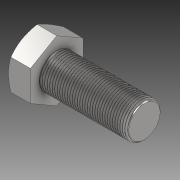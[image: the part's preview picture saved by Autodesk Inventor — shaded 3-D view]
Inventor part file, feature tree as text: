
AUTODESK INVENTOR PART (.ipt)
format: ipt  version: 2020 (Build 240168000, 168)  size: 557,568 bytes
history: mixed  units: in
note: dims shown in document units (in); Inventor stores cm internally (conversion verified against a paired STEP export)
features: revolve x1, imported_body x1
ambient origin geometry x8: Origin, YZ Plane, XZ Plane, XY Plane, X Axis, Y Axis, Z Axis, Center Point
bodies: Solid1 (imported_parasolid)
feature tree (2):
  revolve  "Revolve1"  [1 undecoded]
  imported_body  NMx_Import_Brep_tag  [imported B-rep: ~3 faces, bbox_mm=None]
note: 1 required parameter value undecoded (feature->parameter linkage not recoverable at this tier; creation-order binding heuristic only, values carry confidence <= 0.55)
